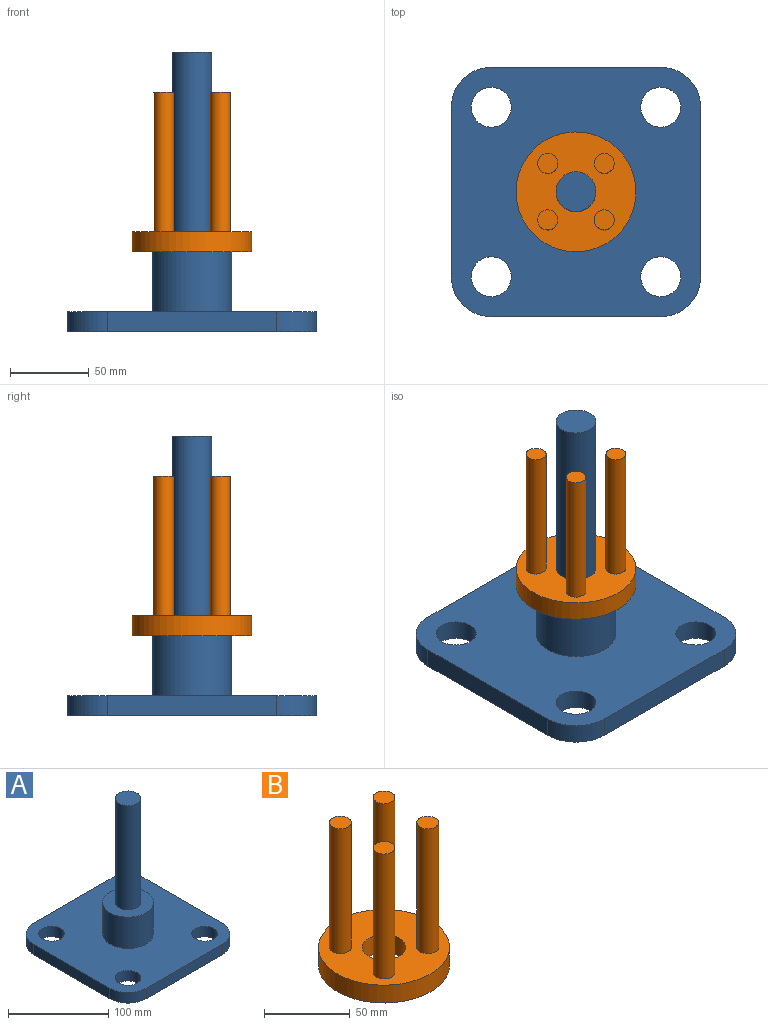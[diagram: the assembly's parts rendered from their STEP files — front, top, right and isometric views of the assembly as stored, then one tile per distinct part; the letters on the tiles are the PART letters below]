
ASSEMBLY  parts=2 mates=1
PART A: 18 faces, bbox 158.6x158.6x177.8 mm
  f0: cylinder r=25.4mm len=25.4mm, axis (0,0,-1), area 506.7mm2, adj f1,f10,f12,f13
  f1: plane 107.76x12.7mm, normal (0,-1,0), area 1368.6mm2, adj f0,f2,f12,f13
  f2: cylinder r=25.4mm len=25.4mm, axis (0,0,-1), area 506.7mm2, adj f1,f3,f12,f13
  f3: plane 107.76x12.7mm, normal (1,0,0), area 1368.6mm2, adj f2,f4,f12,f13
  f4: cylinder r=25.4mm len=25.4mm, axis (0,0,-1), area 506.7mm2, adj f3,f5,f12,f13
  f5: plane 107.76x12.7mm, normal (0,1,0), area 1368.6mm2, adj f4,f6,f12,f13
  f6: cylinder r=25.4mm len=25.4mm, axis (0,0,-1), area 506.7mm2, adj f5,f10,f12,f13
  f7: cylinder r=12.7mm len=25.4mm, axis (0,0,-1), area 1013.4mm2, adj f12,f13
  f8: cylinder r=12.7mm len=25.4mm, axis (0,0,-1), area 1013.4mm2, adj f12,f13
  f9: cylinder r=12.7mm len=25.4mm, axis (0,0,-1), area 1013.4mm2, adj f12,f13
  f10: plane 107.76x12.7mm, normal (-1,0,0), area 1368.6mm2, adj f0,f6,f12,f13
  f11: cylinder r=12.7mm len=25.4mm, axis (0,0,-1), area 1013.4mm2, adj f12,f13
  f12: plane 158.56x158.56mm, normal (0,0,1), area 20534.8mm2, adj f0,f1,f2,f3,f4,f5,f6,f7
  f13: plane 158.56x158.56mm, normal (0,0,-1), area 22561.6mm2, adj f0,f1,f2,f3,f4,f5,f6,f7
  f14: cylinder r=25.4mm len=50.8mm, axis (0,0,-1), area 6080.5mm2, adj f12,f15
  f15: plane 50.8x50.8mm, normal (0,0,1), area 1520.1mm2, adj f14,f16
  f16: cylinder r=12.7mm len=127mm, axis (0,0,-1), area 10134.1mm2, adj f15,f17
  f17: plane 25.4x25.4mm, normal (0,0,1), area 506.7mm2, adj f16
PART B: 12 faces, bbox 76.2x76.2x101.6 mm
  f0: cylinder r=12.7mm len=25.4mm, axis (0,0,-1), area 1013.4mm2, adj f2,f3
  f1: cylinder r=38.1mm len=76.2mm, axis (0,0,-1), area 3040.2mm2, adj f2,f3
  f2: plane 76.2x76.2mm, normal (0,0,1), area 3547mm2, adj f0,f1,f4,f6,f8,f10
  f3: plane 76.2x76.2mm, normal (0,0,-1), area 4053.7mm2, adj f0,f1
  f4: cylinder r=6.35mm len=88.9mm, axis (0,0,-1), area 3547mm2, adj f2,f5
  f5: plane 12.7x12.7mm, normal (0,0,1), area 126.7mm2, adj f4
  f6: cylinder r=6.35mm len=88.9mm, axis (0,0,-1), area 3547mm2, adj f2,f7
  f7: plane 12.7x12.7mm, normal (0,0,1), area 126.7mm2, adj f6
  f8: cylinder r=6.35mm len=88.9mm, axis (0,0,-1), area 3547mm2, adj f2,f9
  f9: plane 12.7x12.7mm, normal (0,0,1), area 126.7mm2, adj f8
  f10: cylinder r=6.35mm len=88.9mm, axis (0,0,-1), area 3547mm2, adj f2,f11
  f11: plane 12.7x12.7mm, normal (0,0,1), area 126.7mm2, adj f10
PLACE A t=(-47.92,-4.43,-16.97)mm
PLACE B t=(-47.92,-4.43,33.83)mm
MATE fastened B.f0 <-> A.f14  axis (0,0,-1) through (-47.92,-4.43,33.83)mm
